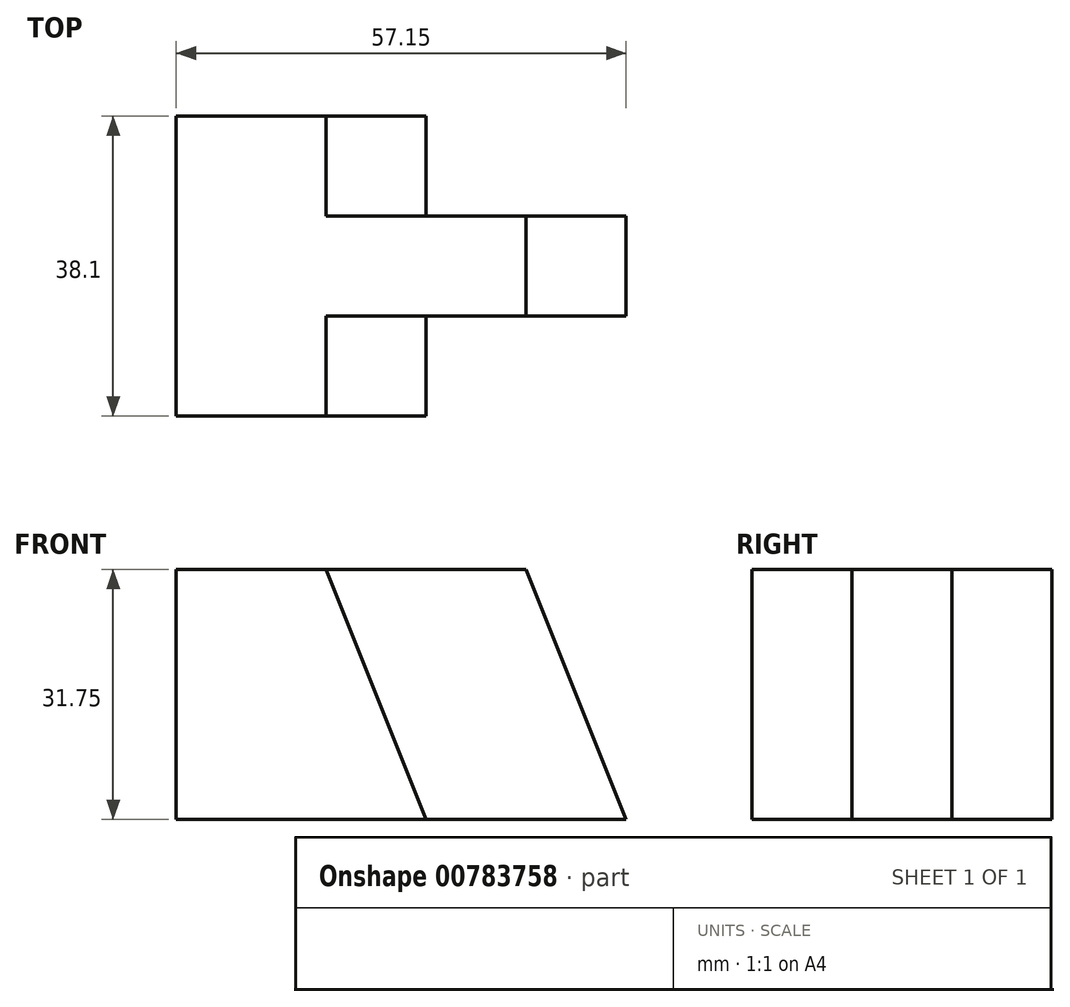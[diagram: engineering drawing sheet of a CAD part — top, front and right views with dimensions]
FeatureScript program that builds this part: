
annotation { "Feature Type Name" : "Feature", "Feature Type Description" : "" }
export const myFeature = defineFeature(function(context is Context, id is Id, definition is map)
    precondition{}
    {
        {
            var Q0;
            Q0=qCreatedBy(makeId("Front.planeOp"),FACE);
            var sketch = newSketch(context, id + "F0", { "sketchPlane" : qUnion([Q0])});
            skLineSegment(sketch, "E0", {"start": v(0, 0) * mm, "end": v(31.75, 0) * mm});
            skLineSegment(sketch, "E1", {"start": v(31.75, 0) * mm, "end": v(57.15, 0) * mm});
            skLineSegment(sketch, "E2", {"start": v(0, 0) * mm, "end": v(0, 31.75) * mm});
            skLineSegment(sketch, "E3", {"start": v(0, 31.75) * mm, "end": v(19.05, 31.75) * mm});
            skLineSegment(sketch, "E4", {"start": v(19.05, 31.75) * mm, "end": v(31.75, 0) * mm});
            skLineSegment(sketch, "E5", {"start": v(57.15, 0) * mm, "end": v(57.15, 31.75) * mm});
            skLineSegment(sketch, "E6", {"start": v(57.15, 31.75) * mm, "end": v(19.05, 31.75) * mm});
            skSolve(sketch);
        }
        {
            var Q0;
            Q0 = qSketchRegion(id + "F0", true);
            extrude(context, id + "F1", {"entities" : qUnion([Q0]), "depth" : 38.1 * mm, "offsetDistance" : 25.4 * mm});
        }
        {
            var Q0;
            Q0=makeQuery(id+"F1.opExtrude","CAP_FACE",FACE,{"disambiguationData":[OSD([sQuery(id+"F0.wireOp",EDGE,"E0"),sQuery(id+"F0.wireOp",EDGE,"E1"),sQuery(id+"F0.wireOp",EDGE,"E2"),sQuery(id+"F0.wireOp",EDGE,"E3"),sQuery(id+"F0.wireOp",EDGE,"E5"),sQuery(id+"F0.wireOp",EDGE,"E6")])],"isStart":false});
            var sketch = newSketch(context, id + "F2", { "sketchPlane" : qUnion([Q0])});
            skLineSegment(sketch, "E7", {"start": v(0, 31.75) * mm, "end": v(19.05, 31.75) * mm});
            skLineSegment(sketch, "E8", {"start": v(0, 0) * mm, "end": v(31.75, 0) * mm});
            skLineSegment(sketch, "E9", {"start": v(31.75, 0) * mm, "end": v(19.05, 31.75) * mm});
            skSolve(sketch);
        }
        {
            var Q0;
            {var subQ0=sQuery(id+"F2.wireOp",EDGE,"E9");Q0=makeQuery(id+"F2.imprint","IMPRINT",FACE,{"disambiguationData":[TD([[makeQuery(id+"F2.imprint","IMPRINT",EDGE,{"derivedFrom":subQ0}),-1.0]])]});}
            extrude(context, id + "F3", {"entities" : qUnion([Q0]), "operationType" : NewBodyOperationType.REMOVE, "oppositeDirection" : true, "depth" : 12.7 * mm, "offsetDistance" : 25.4 * mm});
        }
        {
            var Q0;
            Q0=makeQuery(id+"F1.opExtrude","SWEPT_FACE",FACE,{"disambiguationData":[OSD([sQuery(id+"F0.wireOp",EDGE,"E5")])]});
            extrude(context, id + "F4", {"entities" : qUnion([Q0]), "operationType" : NewBodyOperationType.REMOVE, "oppositeDirection" : true, "depth" : 57.15 * mm, "offsetDistance" : 25.4 * mm});
        }
        {
            var Q0;
            Q0=makeQuery(id+"F1.opExtrude","CAP_FACE",FACE,{"disambiguationData":[OSD([sQuery(id+"F0.wireOp",EDGE,"E0"),sQuery(id+"F0.wireOp",EDGE,"E1"),sQuery(id+"F0.wireOp",EDGE,"E2"),sQuery(id+"F0.wireOp",EDGE,"E3"),sQuery(id+"F0.wireOp",EDGE,"E5"),sQuery(id+"F0.wireOp",EDGE,"E6")])],"isStart":false});
            var sketch = newSketch(context, id + "F5", { "sketchPlane" : qUnion([Q0])});
            skLineSegment(sketch, "E10", {"start": v(19.05, 31.75) * mm, "end": v(44.45, 31.75) * mm});
            skLineSegment(sketch, "E11", {"start": v(31.75, 0) * mm, "end": v(57.15, 0) * mm});
            skLineSegment(sketch, "E12", {"start": v(57.15, 0) * mm, "end": v(44.45, 31.75) * mm});
            skSolve(sketch);
        }
        {
            var Q0;
            Q0=makeQuery(id+"F5.imprint","IMPRINT",FACE,{"disambiguationData":[TD([[makeQuery(id+"F5.imprint","IMPRINT",EDGE,{"derivedFrom":sQuery(id+"F5.wireOp",EDGE,"E10")}),-1.0]])]});
            var Q1;
            Q1=makeQuery(id+"F5.imprint","IMPRINT",FACE,{"disambiguationData":[TD([[makeQuery(id+"F5.imprint","IMPRINT",EDGE,{"derivedFrom":makeQuery(id+"F1.opExtrude","CAP_EDGE",EDGE,{"disambiguationData":[OSD([sQuery(id+"F0.wireOp",EDGE,"E2")])],"isStart":false})}),-1.0]])]});
            extrude(context, id + "F6", {"entities" : qUnion([Q0, Q1]), "operationType" : NewBodyOperationType.ADD, "depth" : 12.7 * mm, "offsetDistance" : 25.4 * mm});
        }
        {
            var Q0;
            Q0=makeQuery(id+"F6.opExtrude","CAP_FACE",FACE,{"disambiguationData":[OSD([sQuery(id+"F0.wireOp",EDGE,"E0"),sQuery(id+"F0.wireOp",EDGE,"E1"),sQuery(id+"F0.wireOp",EDGE,"E2"),sQuery(id+"F0.wireOp",EDGE,"E3"),sQuery(id+"F0.wireOp",EDGE,"E6"),sQuery(id+"F5.wireOp",EDGE,"E10"),sQuery(id+"F5.wireOp",EDGE,"E11"),sQuery(id+"F5.wireOp",EDGE,"E12")])],"isStart":false});
            var sketch = newSketch(context, id + "F7", { "sketchPlane" : qUnion([Q0])});
            skLineSegment(sketch, "E13", {"start": v(0, 31.75) * mm, "end": v(19.05, 31.75) * mm});
            skLineSegment(sketch, "E14", {"start": v(0, 0) * mm, "end": v(31.75, 0) * mm});
            skLineSegment(sketch, "E15", {"start": v(31.75, 0) * mm, "end": v(19.05, 31.75) * mm});
            skSolve(sketch);
        }
        {
            var Q0;
            Q0=makeQuery(id+"F7.imprint","IMPRINT",FACE,{"disambiguationData":[TD([[makeQuery(id+"F7.imprint","IMPRINT",EDGE,{"derivedFrom":sQuery(id+"F7.wireOp",EDGE,"E13")}),-1.0]])]});
            extrude(context, id + "F8", {"entities" : qUnion([Q0]), "operationType" : NewBodyOperationType.ADD, "depth" : 12.7 * mm, "offsetDistance" : 25.4 * mm});
        }
    });
